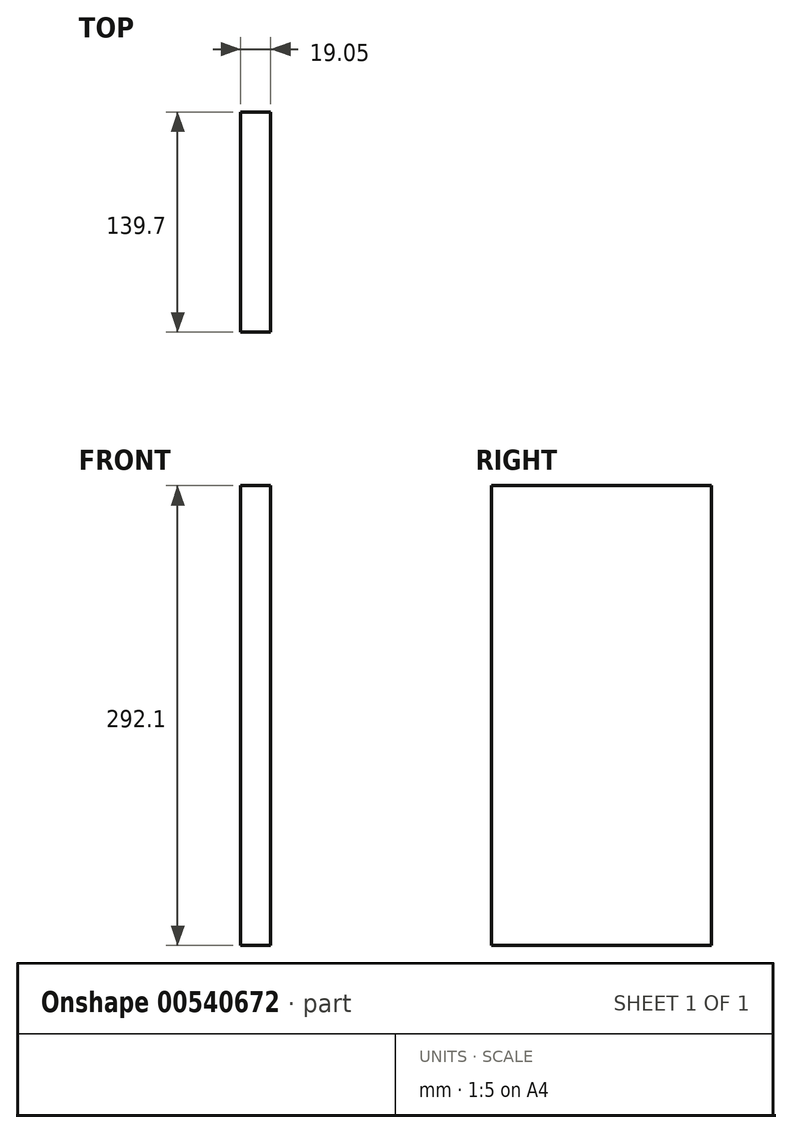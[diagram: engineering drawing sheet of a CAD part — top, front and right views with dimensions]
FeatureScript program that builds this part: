
annotation { "Feature Type Name" : "Feature", "Feature Type Description" : "" }
export const myFeature = defineFeature(function(context is Context, id is Id, definition is map)
    precondition{}
    {
        {
            var Q0;
            Q0=qCreatedBy(makeId("Right.planeOp"),FACE);
            var sketch = newSketch(context, id + "F0", { "sketchPlane" : qUnion([Q0])});
            skLineSegment(sketch, "E0.bottom", {"start": v(-77.71, 129.22) * mm, "end": v(61.99, 129.22) * mm});
            skLineSegment(sketch, "E0.top", {"start": v(-77.71, -162.88) * mm, "end": v(61.99, -162.88) * mm});
            skLineSegment(sketch, "E0.left", {"start": v(-77.71, 129.22) * mm, "end": v(-77.71, -162.88) * mm});
            skLineSegment(sketch, "E0.right", {"start": v(61.99, 129.22) * mm, "end": v(61.99, -162.88) * mm});
            skSolve(sketch);
        }
        {
            var Q0;
            Q0 = qSketchRegion(id + "F0", true);
            extrude(context, id + "F1", {"entities" : qUnion([Q0]), "depth" : 19.05 * mm, "offsetDistance" : 25.4 * mm});
        }
    });
